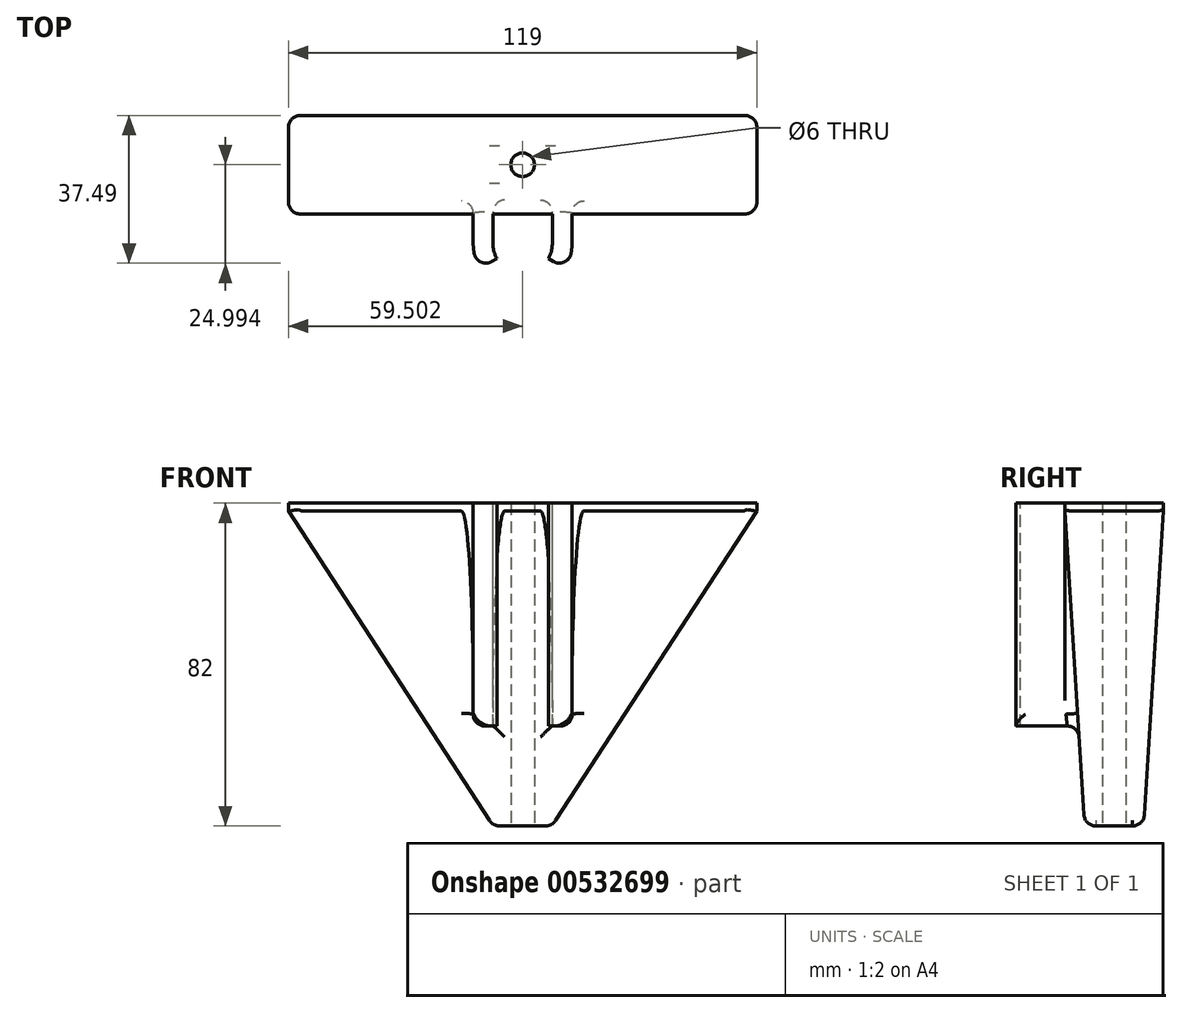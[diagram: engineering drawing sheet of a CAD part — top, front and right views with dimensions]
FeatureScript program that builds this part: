
annotation { "Feature Type Name" : "Feature", "Feature Type Description" : "" }
export const myFeature = defineFeature(function(context is Context, id is Id, definition is map)
    precondition{}
    {
        {
            var Q0;
            Q0=qCreatedBy(makeId("Top.planeOp"),FACE);
            var sketch = newSketch(context, id + "F0", { "sketchPlane" : qUnion([Q0])});
            skLineSegment(sketch, "E0.bottom", {"start": v(-62.43, 31.66) * mm, "end": v(56.57, 31.66) * mm});
            skLineSegment(sketch, "E0.top", {"start": v(-62.43, 6.66) * mm, "end": v(56.57, 6.66) * mm});
            skLineSegment(sketch, "E0.left", {"start": v(-62.43, 31.66) * mm, "end": v(-62.43, 6.66) * mm});
            skLineSegment(sketch, "E0.right", {"start": v(56.57, 31.66) * mm, "end": v(56.57, 6.66) * mm});
            skArc(sketch, "E1", {"start": v(-10.48, -0.9) * mm, "mid": v(-2.93, -8.45) * mm, "end": v(4.62, -0.9) * mm});
            skLineSegment(sketch, "E2", {"start": v(4.62, -0.9) * mm, "end": v(4.62, 6.66) * mm});
            skLineSegment(sketch, "E3", {"start": v(-10.48, -0.9) * mm, "end": v(-10.48, 6.66) * mm});
            skArc(sketch, "E4", {"start": v(-15.48, -0.9) * mm, "mid": v(-2.93, -13.45) * mm, "end": v(9.62, -0.9) * mm});
            skLineSegment(sketch, "E5", {"start": v(-15.48, -0.9) * mm, "end": v(-15.48, 6.66) * mm});
            skLineSegment(sketch, "E6", {"start": v(9.62, -0.9) * mm, "end": v(9.62, 6.66) * mm});
            skLineSegment(sketch, "E7", {"start": v(-9, -4.4) * mm, "end": v(-13.8, -7.17) * mm});
            skLineSegment(sketch, "E8", {"start": v(3.13, -4.4) * mm, "end": v(7.94, -7.17) * mm});
            skLineSegment(sketch, "E9.trimOffspring", {"start": v(-2.93, -7.9) * mm, "end": v(-2.93, -8.45) * mm, "construction": true});
            skLineSegment(sketch, "E10.trimOffspring", {"start": v(-2.93, -13.45) * mm, "end": v(-2.93, -25.46) * mm, "construction": true});
            skPoint(sketch, "E11.start.orphan", {"position": v(-2.93, 6.66) * mm});
            skSolve(sketch);
        }
        {
            var Q0;
            Q0=qCreatedBy(makeId("Top.planeOp"),FACE);
            cPlane(context, id + "F1", {"entities" : qUnion([Q0]), "cplaneType" : CPlaneType.OFFSET, "offset" : 82 * mm, "oppositeDirection" : true, "width" : 150 * mm, "height" : 150 * mm});
        }
        {
            var Q0;
            Q0=qCreatedBy(id+"F1.planeOp",FACE);
            var sketch = newSketch(context, id + "F2", { "sketchPlane" : qUnion([Q0])});
            skLineSegment(sketch, "E12.bottom", {"start": v(-62.43, 31.66) * mm, "end": v(56.57, 31.66) * mm});
            skLineSegment(sketch, "E12.top", {"start": v(-62.43, 6.66) * mm, "end": v(56.57, 6.66) * mm});
            skLineSegment(sketch, "E12.left", {"start": v(-62.43, 31.66) * mm, "end": v(-62.43, 6.66) * mm});
            skLineSegment(sketch, "E12.right", {"start": v(56.57, 31.66) * mm, "end": v(56.57, 6.66) * mm});
            skSolve(sketch);
        }
        {
            var Q0;
            Q0=makeQuery(id+"F2.imprint","IMPRINT",FACE,{"disambiguationData":[TD([[makeQuery(id+"F2.imprint","IMPRINT",EDGE,{"derivedFrom":sQuery(id+"F2.wireOp",EDGE,"E12.bottom")}),-1.0]])]});
            var sketch = newSketch(context, id + "F3", { "sketchPlane" : qUnion([Q0])});
            skLineSegment(sketch, "E13", {"start": v(56.57, 19.16) * mm, "end": v(-62.43, 19.16) * mm, "construction": true});
            skLineSegment(sketch, "E14", {"start": v(-62.43, 19.16) * mm, "end": v(-62.43, 20) * mm, "construction": true});
            skLineSegment(sketch, "E15", {"start": v(-2.93, 6.66) * mm, "end": v(-2.93, 31.66) * mm, "construction": true});
            skSolve(sketch);
        }
        {
            var Q0;
            Q0=makeQuery(id+"F2.imprint","IMPRINT",FACE,{"disambiguationData":[TD([[makeQuery(id+"F2.imprint","IMPRINT",EDGE,{"derivedFrom":sQuery(id+"F2.wireOp",EDGE,"E12.bottom")}),-1.0]])]});
            var sketch = newSketch(context, id + "F4", { "sketchPlane" : qUnion([Q0])});
            skLineSegment(sketch, "E16.bottom", {"start": v(4.57, 26.66) * mm, "end": v(-10.43, 26.66) * mm});
            skLineSegment(sketch, "E16.top", {"start": v(4.57, 11.66) * mm, "end": v(-10.43, 11.66) * mm});
            skLineSegment(sketch, "E16.left", {"start": v(4.57, 26.66) * mm, "end": v(4.57, 11.66) * mm});
            skLineSegment(sketch, "E16.right", {"start": v(-10.43, 26.66) * mm, "end": v(-10.43, 11.66) * mm});
            skPoint(sketch, "E16.middle", {"position": v(-2.93, 19.16) * mm});
            skSolve(sketch);
        }
        {
            var Q0;
            Q0=makeQuery(id+"F0.imprint","IMPRINT",FACE,{"disambiguationData":[TD([[makeQuery(id+"F0.imprint","IMPRINT",EDGE,{"derivedFrom":sQuery(id+"F0.wireOp",EDGE,"E0.bottom")}),-1.0]])]});
            extrude(context, id + "F5", {"entities" : qUnion([Q0]), "oppositeDirection" : true, "depth" : 2 * mm, "offsetDistance" : 25 * mm});
        }
        {
            var Q1;
            Q1=makeQuery(id+"F5.opExtrude","CAP_FACE",FACE,{"disambiguationData":[OSD([sQuery(id+"F0.wireOp",EDGE,"E0.bottom"),sQuery(id+"F0.wireOp",EDGE,"E0.top"),sQuery(id+"F0.wireOp",EDGE,"E0.left"),sQuery(id+"F0.wireOp",EDGE,"E0.right")])],"isStart":false});
            var Q2;
            Q2=makeQuery(id+"F4.imprint","IMPRINT",FACE,{"disambiguationData":[TD([[makeQuery(id+"F4.imprint","IMPRINT",EDGE,{"derivedFrom":sQuery(id+"F4.wireOp",EDGE,"E16.bottom")}),1.0]])]});
            loft(context, id + "F6", {"operationType" : NewBodyOperationType.ADD, "sheetProfilesArray" : [{ "sheetProfileEntities" : qUnion([Q1]) }, { "sheetProfileEntities" : qUnion([Q2]) }]});
        }
        {
            var Q0;
            {var subQ4=sQuery(id+"F0.wireOp",EDGE,"E3");Q0=makeQuery(id+"F0.imprint","IMPRINT",FACE,{"disambiguationData":[TD([[makeQuery(id+"F0.imprint","IMPRINT",EDGE,{"derivedFrom":subQ4}),1.0]])]});}
            var Q1;
            {var subQ0=sQuery(id+"F0.wireOp",EDGE,"E2");Q1=makeQuery(id+"F0.imprint","IMPRINT",FACE,{"disambiguationData":[TD([[makeQuery(id+"F0.imprint","IMPRINT",EDGE,{"derivedFrom":subQ0}),-1.0]])]});}
            extrude(context, id + "F7", {"entities" : qUnion([Q0, Q1]), "operationType" : NewBodyOperationType.ADD, "oppositeDirection" : true, "depth" : 56.6 * mm, "offsetDistance" : 25 * mm});
        }
        {
            var Q0;
            {var subQ0=sQuery(id+"F0.wireOp",EDGE,"E0.top");Q0=makeQuery(id+"F7.opExtrude","SWEPT_FACE",FACE,{"disambiguationData":[OSD([subQ0]),TDD([makeQuery(id+"F0.imprint","IMPRINT",EDGE,{"disambiguationData":[TD([[makeQuery(id+"F0.imprint","INTERSECT",VERTEX,{"derivedFrom":[subQ0,sQuery(id+"F0.wireOp",EDGE,"E3")]}),1.0]])],"derivedFrom":subQ0})])]});}
            var Q1;
            {var subQ0=sQuery(id+"F0.wireOp",EDGE,"E0.top");Q1=makeQuery(id+"F7.opExtrude","SWEPT_FACE",FACE,{"disambiguationData":[OSD([subQ0]),TDD([makeQuery(id+"F0.imprint","IMPRINT",EDGE,{"disambiguationData":[TD([[makeQuery(id+"F0.imprint","INTERSECT",VERTEX,{"derivedFrom":[subQ0,sQuery(id+"F0.wireOp",EDGE,"E2")]}),-1.0]])],"derivedFrom":subQ0})])]});}
            extrude(context, id + "F8", {"entities" : qUnion([Q0, Q1]), "operationType" : NewBodyOperationType.ADD, "depth" : 14.8 * mm, "offsetDistance" : 25 * mm});
        }
        {
            var Q0;
            {var subQ0=sQuery(id+"F0.wireOp",EDGE,"E0.top");Q0=makeQuery(id+"F8.boolean.opBoolean","INTERSECT",EDGE,{"derivedFrom":[makeQuery(id+"F6.opLoft","SWEPT_FACE",FACE,{"disambiguationData":[OSD([subQ0,sQuery(id+"F0.wireOp",EDGE,"E0.left"),sQuery(id+"F0.wireOp",EDGE,"E0.right"),sQuery(id+"F4.wireOp",EDGE,"E16.top"),sQuery(id+"F4.wireOp",EDGE,"E16.left"),sQuery(id+"F4.wireOp",EDGE,"E16.right")])]}),makeQuery(id+"F8.opExtrude","SWEPT_FACE",FACE,{"disambiguationData":[OSD([subQ0,sQuery(id+"F0.wireOp",EDGE,"E3")])]})]});}
            var Q1;
            {var subQ0=sQuery(id+"F0.wireOp",EDGE,"E0.top");Q1=makeQuery(id+"F8.boolean.opBoolean","INTERSECT",EDGE,{"derivedFrom":[makeQuery(id+"F6.opLoft","SWEPT_FACE",FACE,{"disambiguationData":[OSD([subQ0,sQuery(id+"F0.wireOp",EDGE,"E0.left"),sQuery(id+"F0.wireOp",EDGE,"E0.right"),sQuery(id+"F4.wireOp",EDGE,"E16.top"),sQuery(id+"F4.wireOp",EDGE,"E16.left"),sQuery(id+"F4.wireOp",EDGE,"E16.right")])]}),makeQuery(id+"F8.opExtrude","SWEPT_FACE",FACE,{"disambiguationData":[OSD([subQ0,sQuery(id+"F0.wireOp",EDGE,"E2")])]})]});}
            var Q2;
            {var subQ0=sQuery(id+"F0.wireOp",EDGE,"E0.top");Q2=makeQuery(id+"F8.boolean.opBoolean","INTERSECT",EDGE,{"derivedFrom":[makeQuery(id+"F6.opLoft","SWEPT_FACE",FACE,{"disambiguationData":[OSD([subQ0,sQuery(id+"F0.wireOp",EDGE,"E0.left"),sQuery(id+"F0.wireOp",EDGE,"E0.right"),sQuery(id+"F4.wireOp",EDGE,"E16.top"),sQuery(id+"F4.wireOp",EDGE,"E16.left"),sQuery(id+"F4.wireOp",EDGE,"E16.right")])]}),makeQuery(id+"F8.opExtrude","SWEPT_FACE",FACE,{"disambiguationData":[OSD([subQ0,sQuery(id+"F0.wireOp",EDGE,"E6")])]})]});}
            var Q3;
            {var subQ0=sQuery(id+"F0.wireOp",EDGE,"E0.top");Q3=makeQuery(id+"F8.boolean.opBoolean","INTERSECT",EDGE,{"derivedFrom":[makeQuery(id+"F6.opLoft","SWEPT_FACE",FACE,{"disambiguationData":[OSD([subQ0,sQuery(id+"F0.wireOp",EDGE,"E0.left"),sQuery(id+"F0.wireOp",EDGE,"E0.right"),sQuery(id+"F4.wireOp",EDGE,"E16.top"),sQuery(id+"F4.wireOp",EDGE,"E16.left"),sQuery(id+"F4.wireOp",EDGE,"E16.right")])]}),makeQuery(id+"F8.opExtrude","SWEPT_FACE",FACE,{"disambiguationData":[OSD([subQ0,sQuery(id+"F0.wireOp",EDGE,"E5")])]})]});}
            var Q4;
            Q4=makeQuery(id+"F6.opLoft","SWEPT_EDGE",EDGE,{"disambiguationData":[OSD([sQuery(id+"F0.wireOp",EDGE,"E0.top"),sQuery(id+"F0.wireOp",EDGE,"E0.right"),sQuery(id+"F4.wireOp",EDGE,"E16.top"),sQuery(id+"F4.wireOp",EDGE,"E16.left")])]});
            var Q5;
            Q5=makeQuery(id+"F6.opLoft","SWEPT_EDGE",EDGE,{"disambiguationData":[OSD([sQuery(id+"F0.wireOp",EDGE,"E0.bottom"),sQuery(id+"F0.wireOp",EDGE,"E0.right"),sQuery(id+"F4.wireOp",EDGE,"E16.bottom"),sQuery(id+"F4.wireOp",EDGE,"E16.left")])]});
            var Q6;
            Q6=makeQuery(id+"F6.opLoft","SWEPT_EDGE",EDGE,{"disambiguationData":[OSD([sQuery(id+"F0.wireOp",EDGE,"E0.bottom"),sQuery(id+"F0.wireOp",EDGE,"E0.left"),sQuery(id+"F4.wireOp",EDGE,"E16.bottom"),sQuery(id+"F4.wireOp",EDGE,"E16.right")])]});
            var Q7;
            Q7=makeQuery(id+"F6.opLoft","SWEPT_EDGE",EDGE,{"disambiguationData":[OSD([sQuery(id+"F0.wireOp",EDGE,"E0.top"),sQuery(id+"F0.wireOp",EDGE,"E0.left"),sQuery(id+"F4.wireOp",EDGE,"E16.top"),sQuery(id+"F4.wireOp",EDGE,"E16.right")])]});
            var Q8;
            Q8=makeQuery(id+"F5.opExtrude","SWEPT_EDGE",EDGE,{"disambiguationData":[OSD([sQuery(id+"F0.wireOp",EDGE,"E0.bottom"),sQuery(id+"F0.wireOp",EDGE,"E0.right")])]});
            var Q9;
            Q9=makeQuery(id+"F5.opExtrude","SWEPT_EDGE",EDGE,{"disambiguationData":[OSD([sQuery(id+"F0.wireOp",EDGE,"E0.top"),sQuery(id+"F0.wireOp",EDGE,"E0.right")])]});
            var Q10;
            Q10=makeQuery(id+"F5.opExtrude","SWEPT_EDGE",EDGE,{"disambiguationData":[OSD([sQuery(id+"F0.wireOp",EDGE,"E0.top"),sQuery(id+"F0.wireOp",EDGE,"E0.left")])]});
            var Q11;
            Q11=makeQuery(id+"F5.opExtrude","SWEPT_EDGE",EDGE,{"disambiguationData":[OSD([sQuery(id+"F0.wireOp",EDGE,"E0.bottom"),sQuery(id+"F0.wireOp",EDGE,"E0.left")])]});
            var Q12;
            Q12=makeQuery(id+"F6.opLoft","MID_CAP_EDGE",EDGE,{"disambiguationData":[OSD([sQuery(id+"F4.wireOp",EDGE,"E16.bottom"),sQuery(id+"F4.wireOp",EDGE,"E16.left"),sQuery(id+"F4.wireOp",EDGE,"E16.right")])],"capPos":1.0});
            var Q13;
            Q13=makeQuery(id+"F6.opLoft","MID_CAP_EDGE",EDGE,{"disambiguationData":[OSD([sQuery(id+"F4.wireOp",EDGE,"E16.bottom"),sQuery(id+"F4.wireOp",EDGE,"E16.top"),sQuery(id+"F4.wireOp",EDGE,"E16.right")])],"capPos":1.0});
            var Q14;
            Q14=makeQuery(id+"F6.opLoft","MID_CAP_EDGE",EDGE,{"disambiguationData":[OSD([sQuery(id+"F4.wireOp",EDGE,"E16.bottom"),sQuery(id+"F4.wireOp",EDGE,"E16.top"),sQuery(id+"F4.wireOp",EDGE,"E16.left")])],"capPos":1.0});
            var Q15;
            Q15=makeQuery(id+"F6.opLoft","MID_CAP_EDGE",EDGE,{"disambiguationData":[OSD([sQuery(id+"F4.wireOp",EDGE,"E16.top"),sQuery(id+"F4.wireOp",EDGE,"E16.left"),sQuery(id+"F4.wireOp",EDGE,"E16.right")])],"capPos":1.0});
            var Q16;
            {var subQ0=sQuery(id+"F0.wireOp",EDGE,"E0.top");Q16=makeQuery(id+"F8.boolean.opBoolean","INTERSECT",EDGE,{"derivedFrom":[makeQuery(id+"F6.opLoft","SWEPT_FACE",FACE,{"disambiguationData":[OSD([subQ0,sQuery(id+"F0.wireOp",EDGE,"E0.left"),sQuery(id+"F0.wireOp",EDGE,"E0.right"),sQuery(id+"F4.wireOp",EDGE,"E16.top"),sQuery(id+"F4.wireOp",EDGE,"E16.left"),sQuery(id+"F4.wireOp",EDGE,"E16.right")])]}),makeQuery(id+"F8.opExtrude","SWEPT_FACE",FACE,{"disambiguationData":[OSD([subQ0]),TDD([makeQuery(id+"F7.opExtrude","CAP_EDGE",EDGE,{"disambiguationData":[OSD([subQ0]),TDD([makeQuery(id+"F0.imprint","IMPRINT",EDGE,{"disambiguationData":[TD([[makeQuery(id+"F0.imprint","INTERSECT",VERTEX,{"derivedFrom":[subQ0,sQuery(id+"F0.wireOp",EDGE,"E3")]}),1.0]])],"derivedFrom":subQ0})])],"isStart":false})])]})]});}
            var Q17;
            {var subQ0=sQuery(id+"F0.wireOp",EDGE,"E0.top");Q17=makeQuery(id+"F8.boolean.opBoolean","INTERSECT",EDGE,{"derivedFrom":[makeQuery(id+"F6.opLoft","SWEPT_FACE",FACE,{"disambiguationData":[OSD([subQ0,sQuery(id+"F0.wireOp",EDGE,"E0.left"),sQuery(id+"F0.wireOp",EDGE,"E0.right"),sQuery(id+"F4.wireOp",EDGE,"E16.top"),sQuery(id+"F4.wireOp",EDGE,"E16.left"),sQuery(id+"F4.wireOp",EDGE,"E16.right")])]}),makeQuery(id+"F8.opExtrude","SWEPT_FACE",FACE,{"disambiguationData":[OSD([subQ0]),TDD([makeQuery(id+"F7.opExtrude","CAP_EDGE",EDGE,{"disambiguationData":[OSD([subQ0]),TDD([makeQuery(id+"F0.imprint","IMPRINT",EDGE,{"disambiguationData":[TD([[makeQuery(id+"F0.imprint","INTERSECT",VERTEX,{"derivedFrom":[subQ0,sQuery(id+"F0.wireOp",EDGE,"E2")]}),-1.0]])],"derivedFrom":subQ0})])],"isStart":false})])]})]});}
            var Q18;
            Q18=makeQuery(id+"F7.opExtrude","SWEPT_EDGE",EDGE,{"disambiguationData":[OSD([sQuery(id+"F0.wireOp",EDGE,"E4"),sQuery(id+"F0.wireOp",EDGE,"E8")])]});
            var Q19;
            Q19=makeQuery(id+"F7.opExtrude","SWEPT_EDGE",EDGE,{"disambiguationData":[OSD([sQuery(id+"F0.wireOp",EDGE,"E4"),sQuery(id+"F0.wireOp",EDGE,"E7")])]});
            var Q20;
            {var subQ0=sQuery(id+"F0.wireOp",EDGE,"E6");Q20=makeQuery(id+"F8.boolean.opBoolean","MERGE",EDGE,{"derivedFrom":[makeQuery(id+"F7.opExtrude","CAP_EDGE",EDGE,{"disambiguationData":[OSD([subQ0])],"isStart":false}),makeQuery(id+"F8.opExtrude","SWEPT_EDGE",EDGE,{"disambiguationData":[OSD([sQuery(id+"F0.wireOp",EDGE,"E0.top"),subQ0])]})]});}
            var Q21;
            {var subQ0=sQuery(id+"F0.wireOp",EDGE,"E5");Q21=makeQuery(id+"F8.boolean.opBoolean","MERGE",EDGE,{"derivedFrom":[makeQuery(id+"F7.opExtrude","CAP_EDGE",EDGE,{"disambiguationData":[OSD([subQ0])],"isStart":false}),makeQuery(id+"F8.opExtrude","SWEPT_EDGE",EDGE,{"disambiguationData":[OSD([sQuery(id+"F0.wireOp",EDGE,"E0.top"),subQ0])]})]});}
            fillet(context, id + "F9", {"entities" : qUnion([Q0, Q1, Q2, Q3, Q4, Q5, Q6, Q7, Q8, Q9, Q10, Q11, Q12, Q13, Q14, Q15, Q16, Q17, Q18, Q19, Q20, Q21]), "radius" : 3 * mm, "tangentPropagation" : true, "allowEdgeOverflow" : false});
        }
        {
            var Q0;
            Q0=makeQuery(id+"F6.opLoft","CAP_FACE",FACE,{"disambiguationData":[OSD([makeQuery(id+"F4.imprint","IMPRINT",FACE,{"disambiguationData":[TD([[makeQuery(id+"F4.imprint","IMPRINT",EDGE,{"derivedFrom":sQuery(id+"F4.wireOp",EDGE,"E16.bottom")}),1.0]])]})])],"isStart":true});
            var sketch = newSketch(context, id + "F10", { "sketchPlane" : qUnion([Q0])});
            skLineSegment(sketch, "E17", {"start": v(-2.93, -14.48) * mm, "end": v(-2.93, -23.85) * mm, "construction": true});
            skCircle(sketch, "E18", {"center": v(-2.93, -19.16) * mm, "radius": 3 * mm});
            skSolve(sketch);
        }
        {
            var Q0;
            Q0 = qSketchRegion(id + "F10", true);
            var Q1;
            {var subQ0=sQuery(id+"F0.wireOp",EDGE,"E4");var subQ1=sQuery(id+"F0.wireOp",EDGE,"E1");var subQ2=sQuery(id+"F0.wireOp",EDGE,"E0.top");Q1=makeQuery(id+"F7.boolean.opBoolean","MERGE",FACE,{"derivedFrom":[makeQuery(id+"F5.opExtrude","CAP_FACE",FACE,{"disambiguationData":[OSD([sQuery(id+"F0.wireOp",EDGE,"E0.bottom"),subQ2,sQuery(id+"F0.wireOp",EDGE,"E0.left"),sQuery(id+"F0.wireOp",EDGE,"E0.right")])],"isStart":true}),makeQuery(id+"F7.opExtrude","CAP_FACE",FACE,{"disambiguationData":[OSD([subQ2,subQ1,sQuery(id+"F0.wireOp",EDGE,"E3"),subQ0,sQuery(id+"F0.wireOp",EDGE,"E5"),sQuery(id+"F0.wireOp",EDGE,"E7")])],"isStart":true}),makeQuery(id+"F7.opExtrude","CAP_FACE",FACE,{"disambiguationData":[OSD([subQ2,subQ1,sQuery(id+"F0.wireOp",EDGE,"E2"),subQ0,sQuery(id+"F0.wireOp",EDGE,"E6"),sQuery(id+"F0.wireOp",EDGE,"E8")])],"isStart":true})]});}
            extrude(context, id + "F11", {"entities" : qUnion([Q0]), "operationType" : NewBodyOperationType.REMOVE, "endBound" : BoundingType.UP_TO_SURFACE, "oppositeDirection" : true, "depth" : 25 * mm, "endBoundEntityFace" : qUnion([Q1]), "offsetDistance" : 25 * mm});
        }
    });
